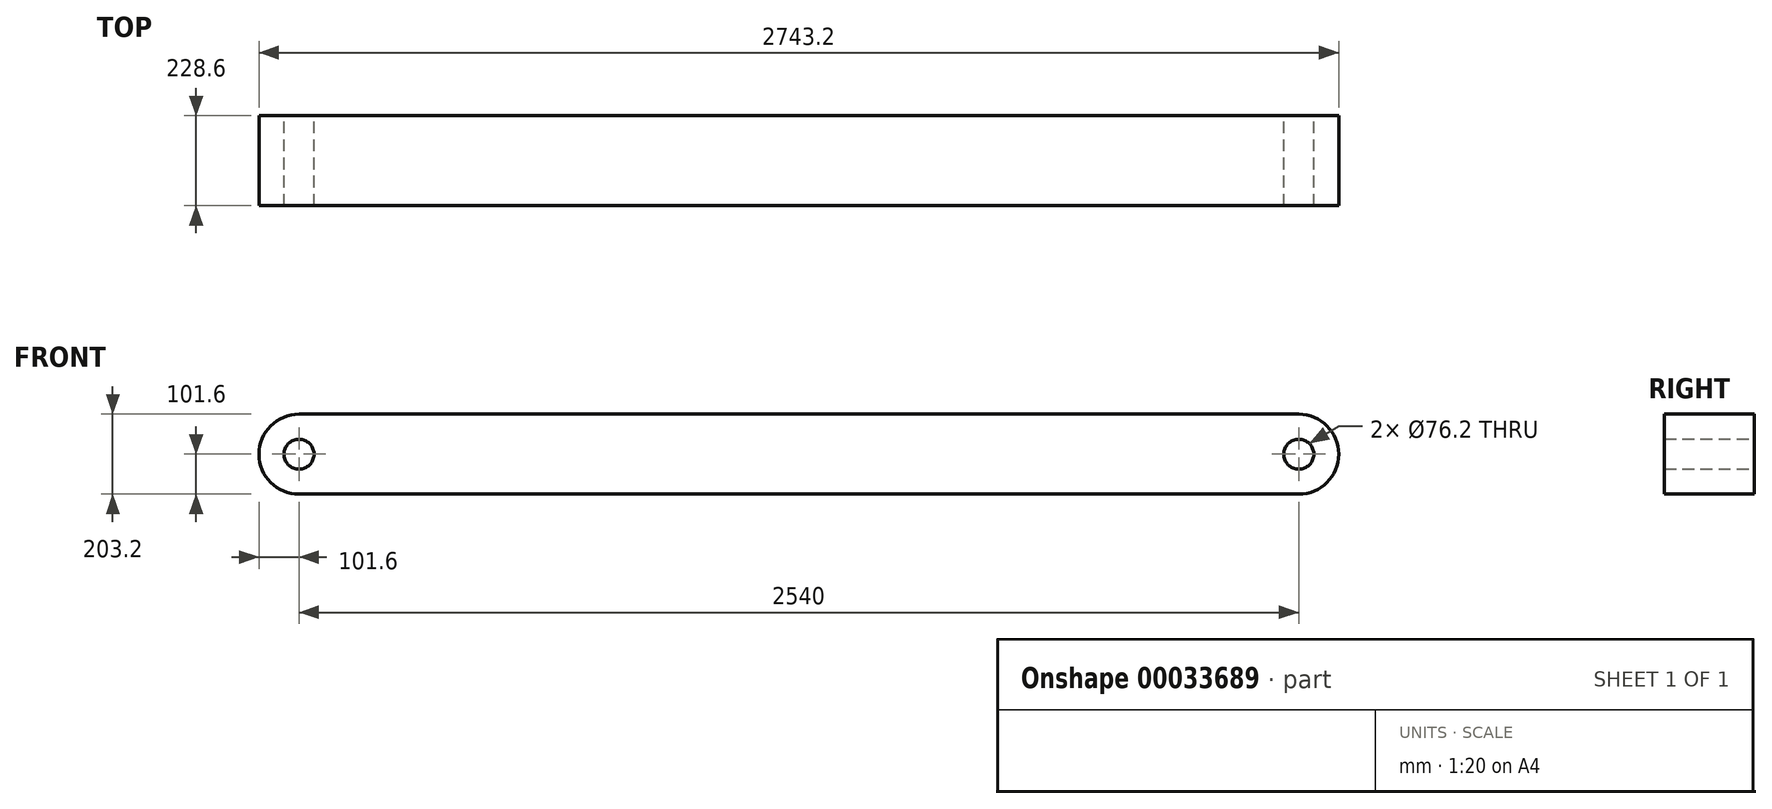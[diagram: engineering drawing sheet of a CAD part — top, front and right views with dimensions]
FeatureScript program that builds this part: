
annotation { "Feature Type Name" : "Feature", "Feature Type Description" : "" }
export const myFeature = defineFeature(function(context is Context, id is Id, definition is map)
    precondition{}
    {
        {
            var Q0;
            Q0=qCreatedBy(makeId("Front.planeOp"),FACE);
            var sketch = newSketch(context, id + "F0", { "sketchPlane" : qUnion([Q0])});
            skLineSegment(sketch, "E0.bottom", {"start": v(0, 0) * mm, "end": v(-2540, 0) * mm});
            skLineSegment(sketch, "E0.top", {"start": v(0, 203.2) * mm, "end": v(-2540, 203.2) * mm});
            skLineSegment(sketch, "E0.left", {"start": v(0, 0) * mm, "end": v(0, 203.2) * mm});
            skLineSegment(sketch, "E0.right", {"start": v(-2540, 0) * mm, "end": v(-2540, 203.2) * mm});
            skCircle(sketch, "E1", {"center": v(-2540, 101.6) * mm, "radius": 101.6 * mm});
            skCircle(sketch, "E2", {"center": v(-2540, 101.6) * mm, "radius": 38.1 * mm});
            skCircle(sketch, "E3", {"center": v(0, 101.6) * mm, "radius": 101.6 * mm});
            skCircle(sketch, "E4", {"center": v(0, 101.6) * mm, "radius": 38.1 * mm});
            skSolve(sketch);
        }
        {
            var Q0;
            Q0 = qSketchRegion(id + "F0", true);
            extrude(context, id + "F1", {"entities" : qUnion([Q0]), "depth" : 228.6 * mm});
        }
    });
